# Revit family: Zumtobel MELLOW LIGHT 6 evo - EB
name_source: partatom
category: Lighting Fixtures
revit_build: Autodesk Revit 2014 (Build: 20140709_2115(x64)
units: mm (PartAtom-declared; Revit-internal decimal feet)

## types (12) — shared parameters
Assembly Code = D5020200
Body = Zumtobel_Metal_White
Color Filter = 16777215
Cover = Zumtobel_Metal_Aluminium
Description = Mellow light recessed luminaire
Dimming Lamp Color Temperature Shift = <None>
Emit Shape Visible in Rendering = No
Lamp = LED
Manufacturer = Zumtobel Lighting
Tilt Angle = 90.00°
Voltage = 230 V
Wings = Zumtobel_PMMA_White
zero-valued in all types: Default Elevation

## per-type parameters (varying)
| type | Apparent Load | Emit from Rectangle Length | Emit from Rectangle Width | Height | Length | Middle Part | Model | Photometric Web File | URL | Width |
| ML evo EA LED3600 M600 L | 33 VA | 1174 mm  [stored 3.85171 ft] | 274 mm  [stored 0.89895 ft] | 82 mm  [stored 0.269029 ft] | 1198 mm  [stored 3.93045 ft] | Zumtobel_PMMA_White_Diffusor | 42185169 | D37750AA_MLevo_EA_LED3600-840_M600L12.ies | http://www.zumtobel.com
42182682 | 298 mm  [stored 0.97769 ft] |
| ML evo EA LED3600 M625 Q | 33 VA | 599 mm | 599 mm | 82 mm  [stored 0.269029 ft] | 623 mm  [stored 2.04396 ft] | Zumtobel_PMMA_White_Diffusor | 42185170 | D37754AA_MLevo_EA_LED3600-840_M625Q.ies | http://www.zumtobel.com
42182682 | 623 mm  [stored 2.04396 ft] |
| ML evo EA LED3600 M625 L | 33 VA | 1224 mm  [stored 4.01575 ft] | 286 mm  [stored 0.93832 ft] | 82 mm  [stored 0.269029 ft] | 1248 mm  [stored 4.09449 ft] | Zumtobel_PMMA_White_Diffusor | 42185171 | D37758AA_MLevo_EA_LED3600-840_M625L12.ies | http://www.zumtobel.com
42182682 | 310 mm  [stored 1.01706 ft] |
| ML evo EA LED3600 M600 Q | 34 VA | 574 mm  [stored 1.8832 ft] | 574 mm  [stored 1.8832 ft] | 77 mm  [stored 0.252625 ft] | 598 mm  [stored 1.96194 ft] | Zumtobel_PMMA_White_Diffusor | 42185168 | D37752AA_MLevo_EA_LED3600-840_M600Q.ies | http://www.zumtobel.com
42182682 | 598 mm  [stored 1.96194 ft] |
| ML evo EL LED3600 M625 Q | 30 VA | 599 mm | 599 mm | 77 mm  [stored 0.252625 ft] | 623 mm  [stored 2.04396 ft] | Zumtobel_PMMA_White | 42184943 | D37802AA_MLevo_EL_LED3600-840_M625Q.ies | http://www.zumtobel.com
42185178 | 623 mm  [stored 2.04396 ft] |
| ML evo EL LED3600 M625 L | 30 VA | 1224 mm  [stored 4.01575 ft] | 286 mm  [stored 0.93832 ft] | 82 mm  [stored 0.269029 ft] | 1248 mm  [stored 4.09449 ft] | Zumtobel_PMMA_White | 42185178 | D37804AA_MLevo_EL_LED3600-840_M625L12.ies | http://www.zumtobel.com
42185178 | 310 mm  [stored 1.01706 ft] |
| ML evo EL LED3600 M600 Q | 30 VA | 574 mm  [stored 1.8832 ft] | 574 mm  [stored 1.8832 ft] | 77 mm  [stored 0.252625 ft] | 598 mm  [stored 1.96194 ft] | Zumtobel_PMMA_White | 42184761 | D37756AA_MLevo_EL_LED3600-840_M600Q.ies | http://www.zumtobel.com
42182682 | 598 mm  [stored 1.96194 ft] |
| ML evo EL LED3600 M600 L | 30 VA | 1174 mm  [stored 3.85171 ft] | 274 mm  [stored 0.89895 ft] | 82 mm  [stored 0.269029 ft] | 1198 mm  [stored 3.93045 ft] | Zumtobel_PMMA_White | 42184760 | D37803AA_MLevo_EL_LED3600-840_M600L12.ies | http://www.zumtobel.com
42182682 | 298 mm  [stored 0.97769 ft] |
| ML evo EA LED4800 M625 Q | 44 VA | 599 mm | 599 mm | 77 mm  [stored 0.252625 ft] | 623 mm  [stored 2.04396 ft] | Zumtobel_PMMA_White_Diffusor | 42184935 | D37754AA_MLevo_EA_LED4800-840_M625Q.ies | http://www.zumtobel.com
42182682 | 623 mm  [stored 2.04396 ft] |
| ML evo EA LED4800 M625 L | 44 VA | 1224 mm  [stored 4.01575 ft] | 286 mm  [stored 0.93832 ft] | 82 mm  [stored 0.269029 ft] | 1248 mm  [stored 4.09449 ft] | Zumtobel_PMMA_White_Diffusor | 42184936 | D37758AA_MLevo_EA_LED4800-840_M625L12.ies | http://www.zumtobel.com
42182682 | 310 mm  [stored 1.01706 ft] |
| ML evo EA LED4800 M600 Q | 45 VA | 574 mm  [stored 1.8832 ft] | 574 mm  [stored 1.8832 ft] | 77 mm  [stored 0.252625 ft] | 598 mm  [stored 1.96194 ft] | Zumtobel_PMMA_White_Diffusor | 42184757 | D37752AA_MLevo_EA_LED4800-840_M600Q.ies | http://www.zumtobel.com
42182682 | 598 mm  [stored 1.96194 ft] |
| ML evo EA LED4800 M600 L | 45 VA | 1174 mm  [stored 3.85171 ft] | 274 mm  [stored 0.89895 ft] | 82 mm  [stored 0.269029 ft] | 1198 mm  [stored 3.93045 ft] | Zumtobel_PMMA_White_Diffusor | 42184756 | D37750AA_MLevo_EA_LED4800-840_M600L12.ies | http://www.zumtobel.com
42182682 | 298 mm  [stored 0.97769 ft] |

note: [stored X ft] marks values corroborated as IEEE doubles in the binary element streams (Revit-internal decimal feet)

## geometry (parser evidence)
native form markers: Sweep x4
no freeform markers — native parametric forms only
